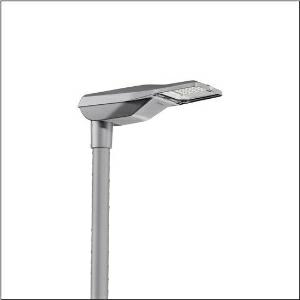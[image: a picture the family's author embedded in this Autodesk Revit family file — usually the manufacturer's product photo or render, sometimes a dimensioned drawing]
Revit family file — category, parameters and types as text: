
# Revit family: streetlight_sl_21_iq_micro___st1_0a_5xe1d31g08cb_12bc
name_source: partatom
category: Lighting Fixtures
units: mm (PartAtom-declared; Revit-internal decimal feet)

## family parameters
Cut with Voids When Loaded = No
Host = Face
Light Source = No
Part Type = Normal
Room Calculation Point = No
Round Connector Dimension = Use Diameter
Shared = No

## types (1)
- --- (1 x LED, 2870 lm, 19.4 W, 3000K)
    Apparent Load = 19 VA
    CIE Flux Codes = 37 72 97 100 100
    Color Rendering = 70
    Color Temperature = 3000K
    Default Elevation = 1800 mm
    Description = Streetlight SL 21 iQ micro, mast luminaire, primary light control with lens, of PMMA, primary optical cover: cover, of toughened safety glass, transparent, light distribution: ST1.0a, light emission: direct distribution, primary light characteristic: asymmetric, installation type: post-top, side-entry, LED, High Power LED, rated luminous flux: 2.870lm, luminous efficacy: 148lm/W, light colour: 730, colour temperature: 3000K, control gear: iQ Street-Remote, control: Street-Remote, Auto-Match, Temp-Guard, Lumen-Switch, Night-Set, Smart-Wire, Light-Fading, Desk-Remote (wireless, voltage-free reading and setting of iQ features in the workshop via application-optimized NFC function/RFID function), optimised constant luminous flux control (CLO 2.0), pre-setting: linear dimming characteristic, mains connection: 220..240V, AC, 50/60Hz, start of lifetime: 19W, end of service life: 20W, reduction: 10W, luminaire housing, of diecast aluminium, powder-coated, SITECO metallic grey (DB 702S), corrosivity category C5 high according to DIN EN ISO 12944, please order mast flange separately, inclination adjustable: 0°, 5°, 10°, 15°, sealing non-destructively replaceable, multi-level sealing system, length: 528mm, width: 235mm, height: 110mm, mast flange for spigot size: 42mm (side-entry): 5XC10008XM4, 60/48mm (side-entry/post-top): 5XC10108XM2, 76/60mm (side-entry/post-top): 5XC10108XM1, protection rating (complete): IP66, insulation class (complete): insulation class II (safety insulation), certification: CE, ENEC, ENEC+, VDE, impact resistance: IK10, permissible operating ambient temperature for outdoor applications: -40..+50°C, standard-compliant lighting for roads and squares, packaging unit: 1 piece

Light Distribution: ST1.0a
    Height = 110 mm
    Lamp = 1 x LED
    Lamp Light Flux = 2870 lm
    Lamp Power = 19.4 W
    Lamp count = 1
    Length = 528 mm
    Luminous efficacy = 148 lm/W
    Manufacturer = Siteco
    ModVariant = No
    Model = 5XE1D31G08CB
    Number of Poles = 1
    OnlyDefault = Yes
    Power Factor = 1
    Product Name = Streetlight SL 21 iQ micro | ST1.0a
    Product group = mast luminaire | pylon top
    ProductGroupID = 6100
    Protection Class = Protection class II
    Protection Degree = IP 66
    RLX_Detail_Level = 1
    RLX_Emergency_Light_Flux = 0 lm
    RLX_Emergency_Type = 0
    RLX_Emergency_Type_DB = No
    RlxData = <blob elided: 98653 chars, md5=efe251a3>
    Socket = socket
    Standby Power = 0 W
    System Light Flux = 2870 lm
    System Power = 19 W
    Type Comments = factory setting: luminous flux: 100 % | dim-lin: 254 | 387 mA
    Type Image = l_1006881.jpg
    URL = http://relux.com
    VarID = @adj_138747
    Voltage = 0 V
    Weight = 0.00 kg
    Width = 235 mm

## geometry (parser evidence)
native form markers: Blend x4, Sweep x9
no freeform markers — native parametric forms only
